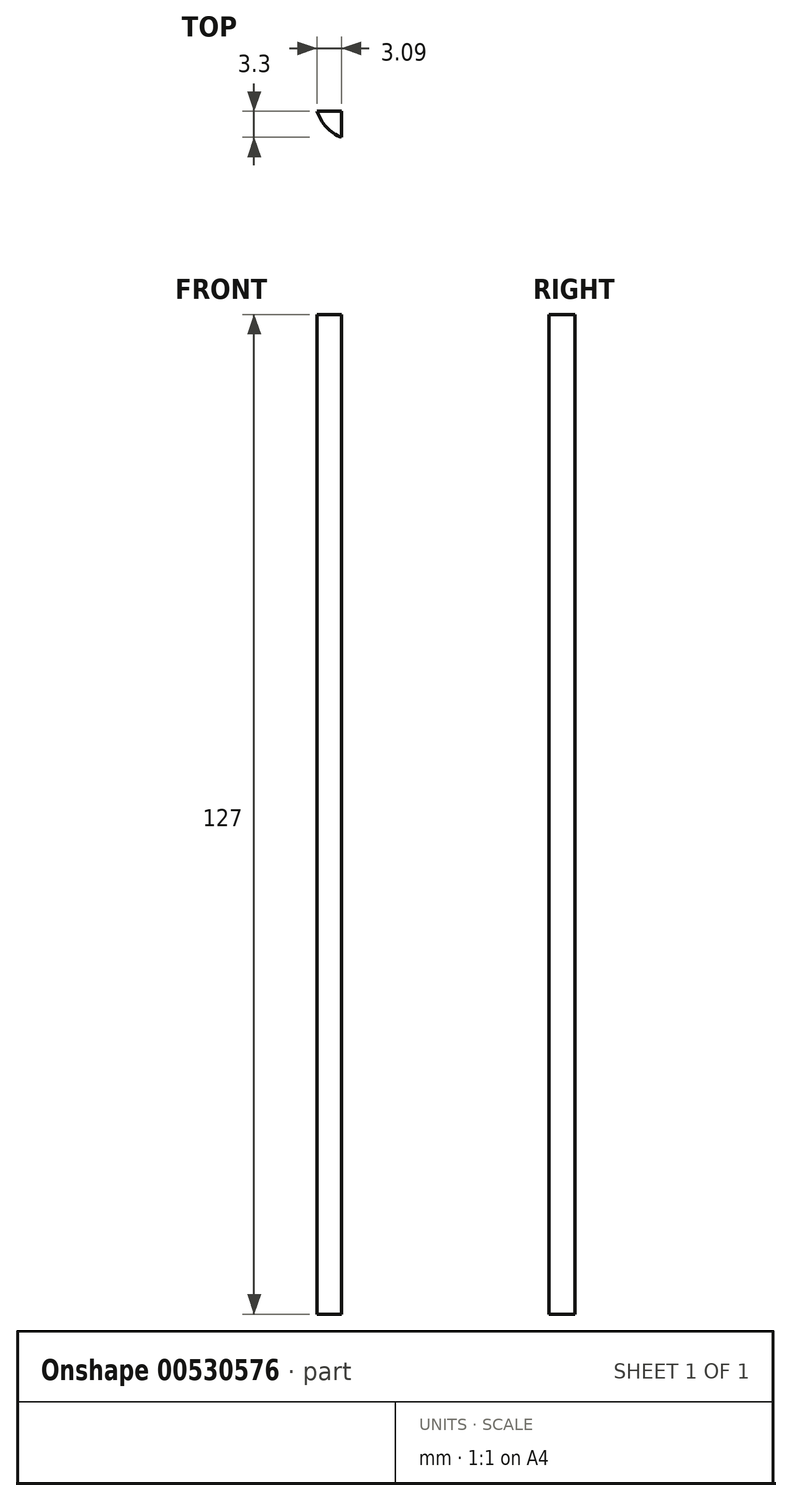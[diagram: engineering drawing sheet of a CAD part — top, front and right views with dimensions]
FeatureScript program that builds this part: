
annotation { "Feature Type Name" : "Feature", "Feature Type Description" : "" }
export const myFeature = defineFeature(function(context is Context, id is Id, definition is map)
    precondition{}
    {
        {
            var Q0;
            Q0=qCreatedBy(makeId("Top.planeOp"),FACE);
            var sketch = newSketch(context, id + "F0", { "sketchPlane" : qUnion([Q0])});
            skLineSegment(sketch, "E0.bottom", {"start": v(1.65, 1.65) * mm, "end": v(-1.65, 1.65) * mm});
            skLineSegment(sketch, "E0.top", {"start": v(1.65, -1.65) * mm, "end": v(-1.65, -1.65) * mm});
            skLineSegment(sketch, "E0.left", {"start": v(1.65, 1.65) * mm, "end": v(1.65, -1.65) * mm});
            skLineSegment(sketch, "E0.right", {"start": v(-1.65, 1.65) * mm, "end": v(-1.65, -1.65) * mm});
            skPoint(sketch, "E0.middle", {"position": v(0, 0) * mm});
            skSolve(sketch);
        }
        {
            var Q0;
            Q0=makeQuery(id+"F0.imprint","IMPRINT",FACE,{"disambiguationData":[TD([[makeQuery(id+"F0.imprint","IMPRINT",EDGE,{"derivedFrom":sQuery(id+"F0.wireOp",EDGE,"E0.bottom")}),1.0]])]});
            extrude(context, id + "F1", {"entities" : qUnion([Q0]), "depth" : 127 * mm, "offsetDistance" : 25.4 * mm});
        }
        {
            var Q0;
            Q0=makeQuery(id+"F1.opExtrude","SWEPT_EDGE",EDGE,{"disambiguationData":[OSD([sQuery(id+"F0.wireOp",EDGE,"E0.top"),sQuery(id+"F0.wireOp",EDGE,"E0.right")])]});
            fillet(context, id + "F2", {"entities" : qUnion([Q0]), "radius" : 5.08 * mm, "tangentPropagation" : true, "allowEdgeOverflow" : false});
        }
    });
